# Revit family: WIR-LVM
name_source: partatom
category: Communication Devices
units: mm (PartAtom-declared; Revit-internal decimal feet)

## family parameters
Cut with Voids When Loaded = No
Host = Face
Maintain Annotation Orientation = No
OmniClass Number = 23.85.80.11.27
OmniClass Title = Lighting Controls
Part Type = Normal
Room Calculation Point = No
Round Connector Dimension = Use Diameter
Shared = Yes

## types (1)
- WIR-LVM
    Assembly Code = D5090
    Certifications = UL: E48166
2.4GHz Version - FCC: U.S. FCC Part 15.247 Class A: OUR-XBEE / OUR-XBEE PRO, Canada IC: 4214A-XBEE / 4214A-XBEE
PRO, Europe CE: ETSI / ETSI
900MHz Version - FCC: U.S. FCC Part 15.247 Class A: MCQ-XB900HP
UL94V-0 Flame retardant ABS or epoxy molding
    Default Elevation = 48 "
    Description = Control Solutions' wiSCAPE® Low Voltage Module is a bi-directional wireless RF device that enables solar (photovoltaic) and battery powered devicesto be managed, monitored and metered. The module adds intelligent functions and networkability to any low-voltage motion sensors, display/text banners and other types of sensors. The module can switch loads up to 1 Amp and features short circuit protection and open load detection. The adaptable sink and source 0-10V output is compatible with all dimming drivers. Digital inputs and an analog output make sending and receiving signals from additional controldevices simple and easy.
    Feartures = 3 Digital inputs / 1 analog input for low-voltage switch, motion and
photo sensors
• Universal dimmer 1-10V (sink/source) for all types of ballasts & drivers
• 1 Secondary dry contact output for driving external loads
• Bi-directional long range wireless RF Mesh communications
• Integration with wiSCAPE software
• Multi-level grouping and multiple scenarios
• Adjustable minimum and maximum dimming levels
• Programmable state after blackout, with peak shaving options
• Blink warning and override before scheduled lights off
• Both locally and remotely controllable with status and metering reporting
• Smart daylight harvesting and motion sensing functions, with occupied
and unoccupied levels including a lamp saver function
• Manual-ON/Auto-OFF, Auto-ON/Auto-OFF and grace period compliant
    Green = Plastic, Gray
    Housing Material = Paint - Carbon Black
    Inputs = 3 Digital: e.g. Motion sensor and switch top/bottom buttons (0-30V) + 1 Analog (0-30V)
    Manufacturer = NX Lighting Controls
    Model = WIR-LVM-IO
    Radio Coverage = Up to ~1,000 ft. (~300m) Note: Antenna must be mounted vertically up or down. Range based on clear line of site.
Recommended deployment practices: Locate wireless devices within a 300 foot radius of the next wireless device for
most reliable performance
    Red = Paint -  Red
    Secondary Output = 1 Digital (supply voltage (12-24V) – max: 20mA) or sink to ground (0V)
    Type Comments = wiSCAPE® Wireless Low Voltage Module
    URL = https://www.currentlighting.com
    Voltage = 12VDC to 24VDC
    Warranty = 5-Years Warranty
    Yellow = Bamboo

## geometry (parser evidence)
native form markers: Sweep x3
no freeform markers — native parametric forms only
